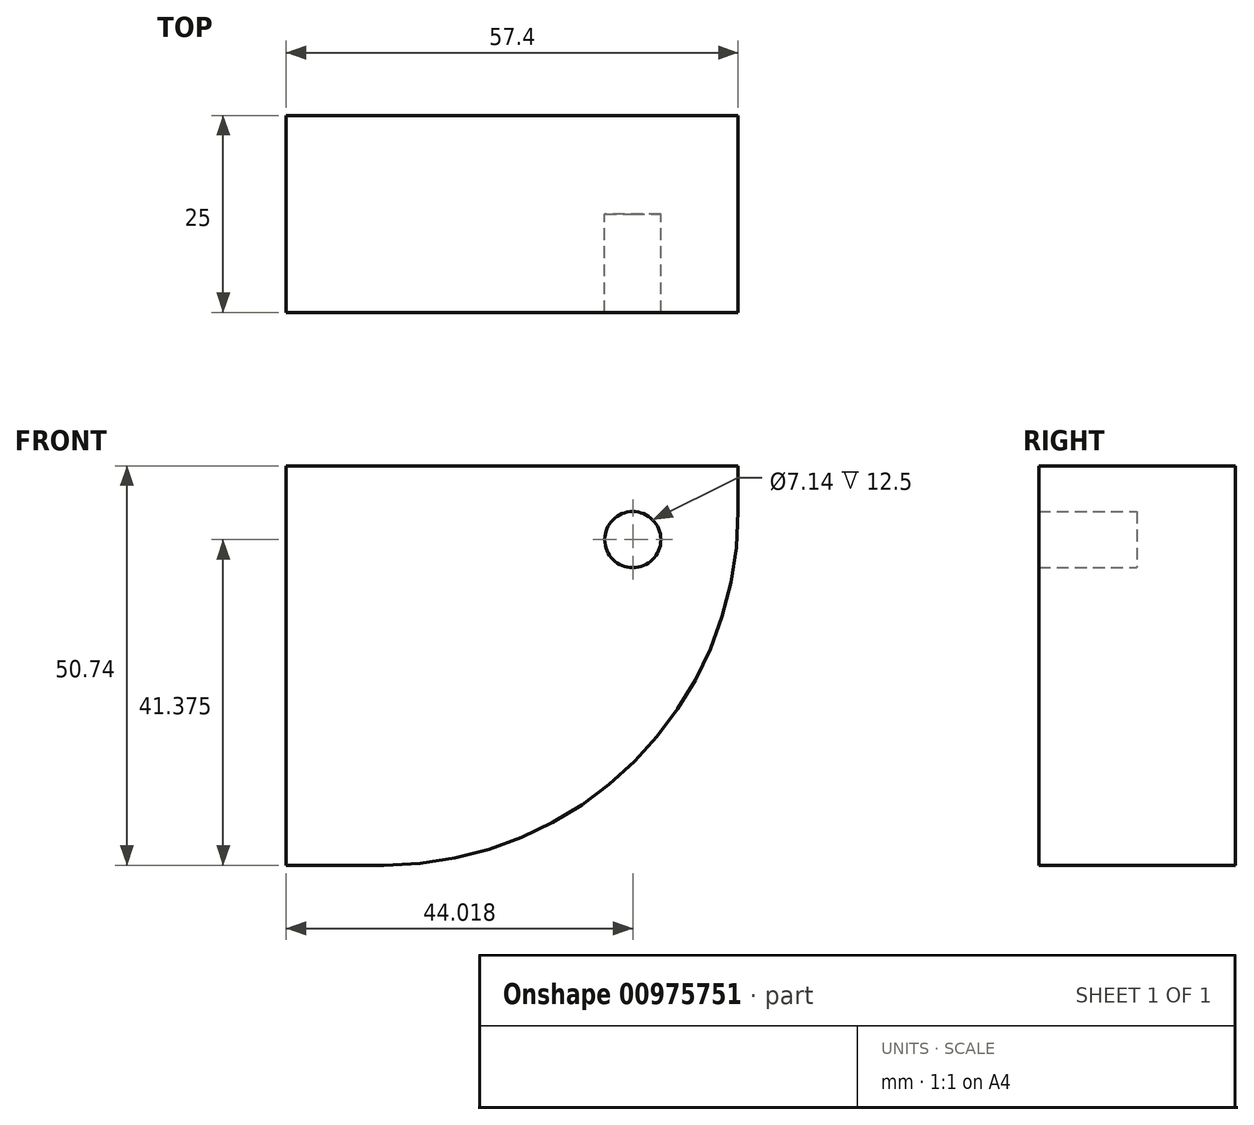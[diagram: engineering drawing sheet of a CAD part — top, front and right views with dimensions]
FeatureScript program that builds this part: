
annotation { "Feature Type Name" : "Feature", "Feature Type Description" : "" }
export const myFeature = defineFeature(function(context is Context, id is Id, definition is map)
    precondition{}
    {
        {
            var Q0;
            Q0=qCreatedBy(makeId("Front.planeOp"),FACE);
            var sketch = newSketch(context, id + "F0", { "sketchPlane" : qUnion([Q0])});
            skLineSegment(sketch, "E0.bottom", {"start": v(28.7, 25.37) * mm, "end": v(-28.7, 25.37) * mm});
            skLineSegment(sketch, "E0.top", {"start": v(28.7, -25.37) * mm, "end": v(-28.7, -25.37) * mm});
            skLineSegment(sketch, "E0.left", {"start": v(28.7, 25.37) * mm, "end": v(28.7, -25.37) * mm});
            skLineSegment(sketch, "E0.right", {"start": v(-28.7, 25.37) * mm, "end": v(-28.7, -25.37) * mm});
            skPoint(sketch, "E0.middle", {"position": v(0, 0) * mm});
            skSolve(sketch);
        }
        {
            var Q0;
            Q0 = qSketchRegion(id + "F0", true);
            extrude(context, id + "F1", {"entities" : qUnion([Q0]), "endBound" : BoundingType.SYMMETRIC, "depth" : 25 * mm, "offsetDistance" : 25 * mm});
        }
        {
            var Q0;
            Q0=qCreatedBy(makeId("Front.planeOp"),FACE);
            var sketch = newSketch(context, id + "F2", { "sketchPlane" : qUnion([Q0])});
            skPoint(sketch, "E1", {"position": v(15.32, 16) * mm});
            skSolve(sketch);
        }
        {
            var Q0;
            Q0=sQuery(id+"F2.wireOp",VERTEX,"E1");
            var Q1;
            Q1=makeQuery(id+"F1.opExtrude","SWEPT_BODY",BODY,{"disambiguationData":[OSD([sQuery(id+"F0.wireOp",EDGE,"E0.bottom"),sQuery(id+"F0.wireOp",EDGE,"E0.top"),sQuery(id+"F0.wireOp",EDGE,"E0.left"),sQuery(id+"F0.wireOp",EDGE,"E0.right")])]});
            hole(context, id + "F3", {"style" : HoleStyle.SIMPLE, "endStyle" : HoleEndStyle.THROUGH, "oppositeDirection" : true, "standardTappedOrClearance" : lookupTablePath({ "fit" : "Normal", "standard" : "Custom", "size" : "1/4", "type" : "Clearance" }), "holeDiameter" : 7.14 * mm, "majorDiameter" : 5 * mm, "isTappedThrough" : true, "tappedDepth" : 12 * mm, "tapClearance" : 3, "locations" : qUnion([Q0]), "scope" : qUnion([Q1])});
        }
        {
            var Q0;
            Q0=makeQuery(id+"F1.opExtrude","SWEPT_EDGE",EDGE,{"disambiguationData":[OSD([sQuery(id+"F0.wireOp",EDGE,"E0.top"),sQuery(id+"F0.wireOp",EDGE,"E0.left")])]});
            fillet(context, id + "F4", {"entities" : qUnion([Q0]), "radius" : 45 * mm, "tangentPropagation" : true, "allowEdgeOverflow" : false});
        }
    });
